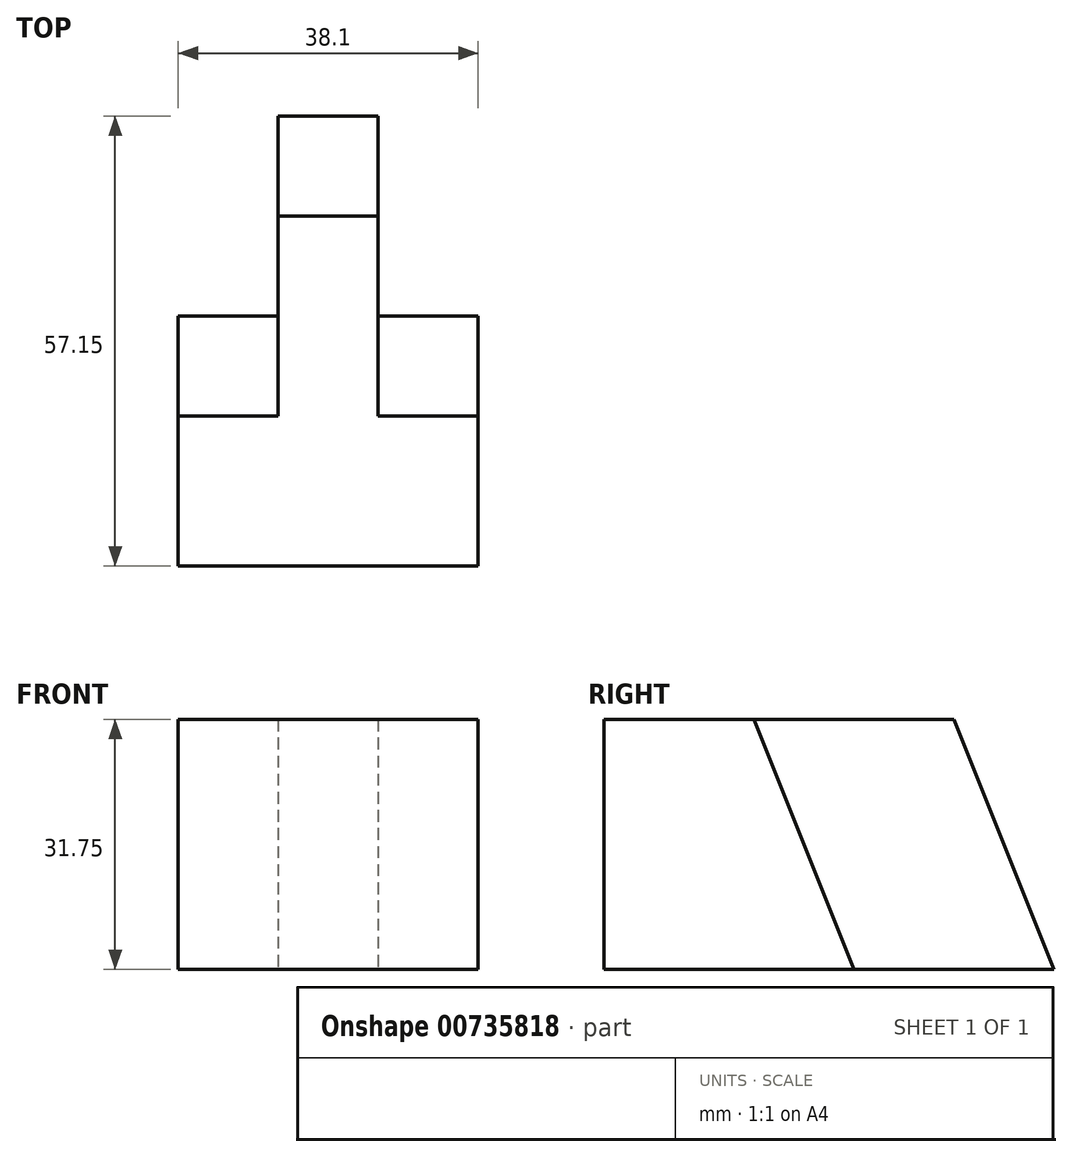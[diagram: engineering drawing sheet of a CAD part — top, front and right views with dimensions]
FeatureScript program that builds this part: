
annotation { "Feature Type Name" : "Feature", "Feature Type Description" : "" }
export const myFeature = defineFeature(function(context is Context, id is Id, definition is map)
    precondition{}
    {
        {
            var Q0;
            Q0=qCreatedBy(makeId("Top.planeOp"),FACE);
            var sketch = newSketch(context, id + "F0", { "sketchPlane" : qUnion([Q0])});
            skLineSegment(sketch, "E0", {"start": v(0, 0) * mm, "end": v(38.1, 0) * mm});
            skLineSegment(sketch, "E1", {"start": v(38.1, 0) * mm, "end": v(38.1, 31.75) * mm});
            skLineSegment(sketch, "E2", {"start": v(38.1, 31.75) * mm, "end": v(25.4, 31.75) * mm});
            skLineSegment(sketch, "E3", {"start": v(25.4, 31.75) * mm, "end": v(25.4, 57.15) * mm});
            skLineSegment(sketch, "E4", {"start": v(25.4, 57.15) * mm, "end": v(12.7, 57.15) * mm});
            skLineSegment(sketch, "E5", {"start": v(12.7, 57.15) * mm, "end": v(12.7, 31.75) * mm});
            skLineSegment(sketch, "E6", {"start": v(12.7, 31.75) * mm, "end": v(0, 31.75) * mm});
            skLineSegment(sketch, "E7", {"start": v(0, 31.75) * mm, "end": v(0, 0) * mm});
            skSolve(sketch);
        }
        {
            var Q0;
            Q0 = qSketchRegion(id + "F0", true);
            extrude(context, id + "F1", {"entities" : qUnion([Q0]), "depth" : 31.75 * mm, "offsetDistance" : 25.4 * mm});
        }
        {
            var Q0;
            Q0=makeQuery(id+"F1.opExtrude","SWEPT_FACE",FACE,{"disambiguationData":[OSD([sQuery(id+"F0.wireOp",EDGE,"E7")])]});
            var sketch = newSketch(context, id + "F2", { "sketchPlane" : qUnion([Q0])});
            skLineSegment(sketch, "E8", {"start": v(-31.75, 0) * mm, "end": v(-31.75, 31.75) * mm});
            skLineSegment(sketch, "E9", {"start": v(-31.75, 31.75) * mm, "end": v(-19.05, 31.75) * mm});
            skLineSegment(sketch, "E10", {"start": v(-19.05, 31.75) * mm, "end": v(-31.75, 0) * mm});
            skSolve(sketch);
        }
        {
            var Q0;
            Q0 = qSketchRegion(id + "F2", true);
            extrude(context, id + "F3", {"entities" : qUnion([Q0]), "operationType" : NewBodyOperationType.REMOVE, "oppositeDirection" : true, "depth" : 12.7 * mm, "offsetDistance" : 25.4 * mm});
        }
        {
            var Q0;
            Q0=makeQuery(id+"F1.opExtrude","SWEPT_FACE",FACE,{"disambiguationData":[OSD([sQuery(id+"F0.wireOp",EDGE,"E1")])]});
            var sketch = newSketch(context, id + "F4", { "sketchPlane" : qUnion([Q0])});
            skLineSegment(sketch, "E11", {"start": v(31.75, 0) * mm, "end": v(31.75, 31.75) * mm});
            skLineSegment(sketch, "E12", {"start": v(31.75, 31.75) * mm, "end": v(19.05, 31.75) * mm});
            skLineSegment(sketch, "E13", {"start": v(19.05, 31.75) * mm, "end": v(31.75, 0) * mm});
            skSolve(sketch);
        }
        {
            var Q0;
            Q0 = qSketchRegion(id + "F4", true);
            extrude(context, id + "F5", {"entities" : qUnion([Q0]), "operationType" : NewBodyOperationType.REMOVE, "oppositeDirection" : true, "depth" : 12.7 * mm, "offsetDistance" : 25.4 * mm});
        }
        {
            var Q0;
            Q0=makeQuery(id+"F5.boolean.opBoolean","MERGE",FACE,{"derivedFrom":[makeQuery(id+"F1.opExtrude","SWEPT_FACE",FACE,{"disambiguationData":[OSD([sQuery(id+"F0.wireOp",EDGE,"E3")])]}),makeQuery(id+"F5.opExtrude","CAP_FACE",FACE,{"disambiguationData":[OSD([sQuery(id+"F4.wireOp",EDGE,"E11"),sQuery(id+"F4.wireOp",EDGE,"E12"),sQuery(id+"F4.wireOp",EDGE,"E13")])],"isStart":false})]});
            var sketch = newSketch(context, id + "F6", { "sketchPlane" : qUnion([Q0])});
            skLineSegment(sketch, "E14", {"start": v(57.15, 31.75) * mm, "end": v(44.45, 31.75) * mm});
            skLineSegment(sketch, "E15", {"start": v(44.45, 31.75) * mm, "end": v(57.15, 0) * mm});
            skLineSegment(sketch, "E16", {"start": v(57.15, 0) * mm, "end": v(57.15, 31.75) * mm});
            skSolve(sketch);
        }
        {
            var Q0;
            Q0 = qSketchRegion(id + "F6", true);
            extrude(context, id + "F7", {"entities" : qUnion([Q0]), "operationType" : NewBodyOperationType.REMOVE, "oppositeDirection" : true, "depth" : 12.7 * mm, "offsetDistance" : 25.4 * mm});
        }
    });
